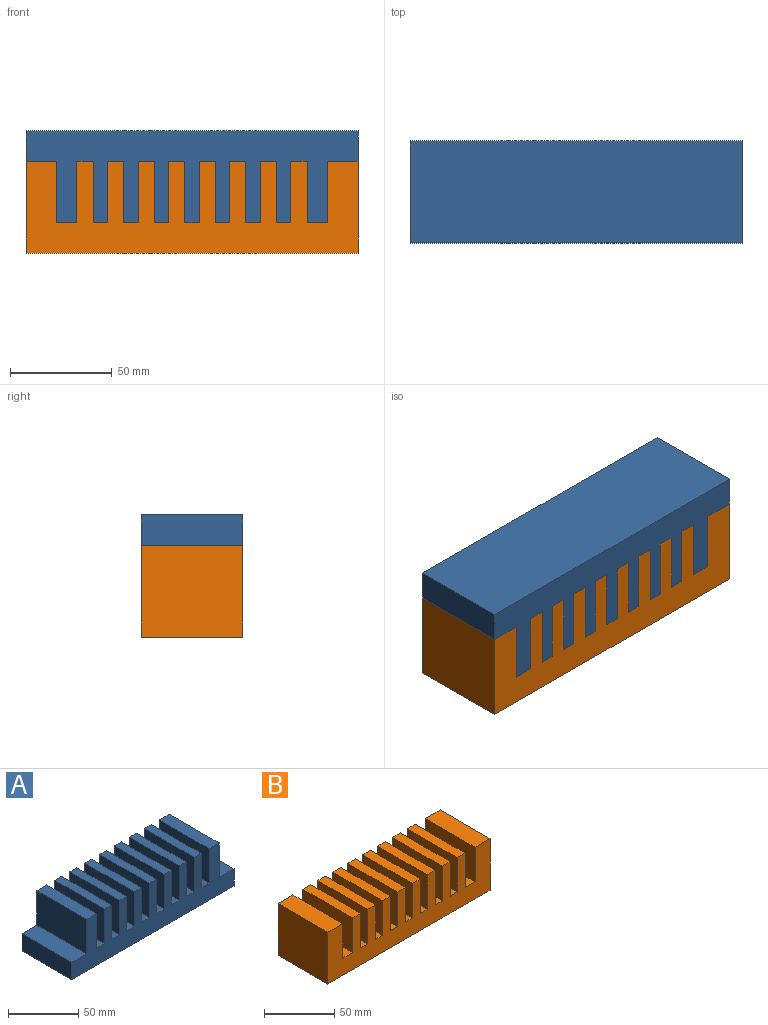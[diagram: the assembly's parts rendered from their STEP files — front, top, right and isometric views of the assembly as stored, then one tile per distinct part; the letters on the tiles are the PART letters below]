
ASSEMBLY  parts=2 mates=1
PART A: 42 faces, bbox 163x50x45 mm
  f0: plane 50x30mm, normal (1,0,0), area 1500mm2, adj f1,f39,f40,f41
  f1: plane 50x7mm, normal (0,0,1), area 350mm2, adj f0,f2,f40,f41
  f2: plane 50x30mm, normal (-1,0,0), area 1500mm2, adj f1,f3,f40,f41
  f3: plane 50x8mm, normal (0,0,1), area 400mm2, adj f2,f4,f40,f41
  f4: plane 50x30mm, normal (1,0,0), area 1500mm2, adj f3,f5,f40,f41
  f5: plane 50x7mm, normal (0,0,1), area 350mm2, adj f4,f6,f40,f41
  f6: plane 50x30mm, normal (-1,0,0), area 1500mm2, adj f5,f7,f40,f41
  f7: plane 50x8mm, normal (0,0,1), area 400mm2, adj f6,f8,f40,f41
  f8: plane 50x30mm, normal (1,0,0), area 1500mm2, adj f7,f9,f40,f41
  f9: plane 50x7mm, normal (0,0,1), area 350mm2, adj f8,f10,f40,f41
  f10: plane 50x30mm, normal (-1,0,0), area 1500mm2, adj f9,f11,f40,f41
  f11: plane 50x8mm, normal (0,0,1), area 400mm2, adj f10,f12,f40,f41
  f12: plane 50x30mm, normal (1,0,0), area 1500mm2, adj f11,f13,f40,f41
  f13: plane 50x7mm, normal (0,0,1), area 350mm2, adj f12,f14,f40,f41
  f14: plane 50x30mm, normal (-1,0,0), area 1500mm2, adj f13,f15,f40,f41
  f15: plane 50x8mm, normal (0,0,1), area 400mm2, adj f14,f16,f40,f41
  f16: plane 50x30mm, normal (1,0,0), area 1500mm2, adj f15,f17,f40,f41
  f17: plane 50x10mm, normal (0,0,1), area 500mm2, adj f16,f18,f40,f41
  f18: plane 50x30mm, normal (-1,0,0), area 1500mm2, adj f17,f19,f40,f41
  f19: plane 50x15mm, normal (0,0,1), area 750mm2, adj f18,f20,f40,f41
  f20: plane 50x15mm, normal (-1,0,0), area 750mm2, adj f19,f21,f40,f41
  f21: plane 163x50mm, normal (0,0,-1), area 8150mm2, adj f20,f22,f40,f41
  f22: plane 50x15mm, normal (1,0,0), area 750mm2, adj f21,f23,f40,f41
  f23: plane 50x15mm, normal (0,0,1), area 750mm2, adj f22,f24,f40,f41
  f24: plane 50x30mm, normal (1,0,0), area 1500mm2, adj f23,f25,f40,f41
  f25: plane 50x10mm, normal (0,0,1), area 500mm2, adj f24,f26,f40,f41
  f26: plane 50x30mm, normal (-1,0,0), area 1500mm2, adj f25,f27,f40,f41
  f27: plane 50x8mm, normal (0,0,1), area 400mm2, adj f26,f28,f40,f41
  f28: plane 50x30mm, normal (1,0,0), area 1500mm2, adj f27,f29,f40,f41
  f29: plane 50x7mm, normal (0,0,1), area 350mm2, adj f28,f30,f40,f41
  f30: plane 50x30mm, normal (-1,0,0), area 1500mm2, adj f29,f31,f40,f41
  f31: plane 50x8mm, normal (0,0,1), area 400mm2, adj f30,f32,f40,f41
  f32: plane 50x30mm, normal (1,0,0), area 1500mm2, adj f31,f33,f40,f41
  f33: plane 50x7mm, normal (0,0,1), area 350mm2, adj f32,f34,f40,f41
  f34: plane 50x30mm, normal (-1,0,0), area 1500mm2, adj f33,f35,f40,f41
  f35: plane 50x8mm, normal (0,0,1), area 400mm2, adj f34,f36,f40,f41
  f36: plane 50x30mm, normal (1,0,0), area 1500mm2, adj f35,f37,f40,f41
  f37: plane 50x7mm, normal (0,0,1), area 350mm2, adj f36,f38,f40,f41
  f38: plane 50x30mm, normal (-1,0,0), area 1500mm2, adj f37,f39,f40,f41
  f39: plane 50x8mm, normal (0,0,1), area 400mm2, adj f0,f38,f40,f41
  f40: plane 163x45mm, normal (0,-1,0), area 4515mm2, adj f0,f1,f2,f3,f4,f5,f6,f7
  f41: plane 163x45mm, normal (0,1,0), area 4515mm2, adj f0,f1,f2,f3,f4,f5,f6,f7
PART B: 42 faces, bbox 163x50x45 mm
  f0: plane 50x7mm, normal (0,0,1), area 350mm2, adj f1,f39,f40,f41
  f1: plane 50x30mm, normal (1,0,0), area 1500mm2, adj f0,f2,f40,f41
  f2: plane 50x8mm, normal (0,0,1), area 400mm2, adj f1,f3,f40,f41
  f3: plane 50x30mm, normal (-1,0,0), area 1500mm2, adj f2,f4,f40,f41
  f4: plane 50x7mm, normal (0,0,1), area 350mm2, adj f3,f5,f40,f41
  f5: plane 50x30mm, normal (1,0,0), area 1500mm2, adj f4,f6,f40,f41
  f6: plane 50x8mm, normal (0,0,1), area 400mm2, adj f5,f7,f40,f41
  f7: plane 50x30mm, normal (-1,0,0), area 1500mm2, adj f6,f8,f40,f41
  f8: plane 50x7mm, normal (0,0,1), area 350mm2, adj f7,f9,f40,f41
  f9: plane 50x30mm, normal (1,0,0), area 1500mm2, adj f8,f10,f40,f41
  f10: plane 50x8mm, normal (0,0,1), area 400mm2, adj f9,f11,f40,f41
  f11: plane 50x30mm, normal (-1,0,0), area 1500mm2, adj f10,f12,f40,f41
  f12: plane 50x7mm, normal (0,0,1), area 350mm2, adj f11,f13,f40,f41
  f13: plane 50x30mm, normal (1,0,0), area 1500mm2, adj f12,f14,f40,f41
  f14: plane 50x8mm, normal (0,0,1), area 400mm2, adj f13,f15,f40,f41
  f15: plane 50x30mm, normal (-1,0,0), area 1500mm2, adj f14,f16,f40,f41
  f16: plane 50x10mm, normal (0,0,1), area 500mm2, adj f15,f17,f40,f41
  f17: plane 50x30mm, normal (1,0,0), area 1500mm2, adj f16,f18,f40,f41
  f18: plane 50x15mm, normal (0,0,1), area 750mm2, adj f17,f19,f40,f41
  f19: plane 50x45mm, normal (-1,0,0), area 2250mm2, adj f18,f20,f40,f41
  f20: plane 163x50mm, normal (0,0,-1), area 8150mm2, adj f19,f21,f40,f41
  f21: plane 50x45mm, normal (1,0,0), area 2250mm2, adj f20,f22,f40,f41
  f22: plane 50x15mm, normal (0,0,1), area 750mm2, adj f21,f23,f40,f41
  f23: plane 50x30mm, normal (-1,0,0), area 1500mm2, adj f22,f24,f40,f41
  f24: plane 50x10mm, normal (0,0,1), area 500mm2, adj f23,f25,f40,f41
  f25: plane 50x30mm, normal (1,0,0), area 1500mm2, adj f24,f26,f40,f41
  f26: plane 50x8mm, normal (0,0,1), area 400mm2, adj f25,f27,f40,f41
  f27: plane 50x30mm, normal (-1,0,0), area 1500mm2, adj f26,f28,f40,f41
  f28: plane 50x7mm, normal (0,0,1), area 350mm2, adj f27,f29,f40,f41
  f29: plane 50x30mm, normal (1,0,0), area 1500mm2, adj f28,f30,f40,f41
  f30: plane 50x8mm, normal (0,0,1), area 400mm2, adj f29,f31,f40,f41
  f31: plane 50x30mm, normal (-1,0,0), area 1500mm2, adj f30,f32,f40,f41
  f32: plane 50x7mm, normal (0,0,1), area 350mm2, adj f31,f33,f40,f41
  f33: plane 50x30mm, normal (1,0,0), area 1500mm2, adj f32,f34,f40,f41
  f34: plane 50x8mm, normal (0,0,1), area 400mm2, adj f33,f35,f40,f41
  f35: plane 50x30mm, normal (-1,0,0), area 1500mm2, adj f34,f36,f40,f41
  f36: plane 50x7mm, normal (0,0,1), area 350mm2, adj f35,f37,f40,f41
  f37: plane 50x30mm, normal (1,0,0), area 1500mm2, adj f36,f38,f40,f41
  f38: plane 50x8mm, normal (0,0,1), area 400mm2, adj f37,f39,f40,f41
  f39: plane 50x30mm, normal (-1,0,0), area 1500mm2, adj f0,f38,f40,f41
  f40: plane 163x45mm, normal (0,-1,0), area 5265mm2, adj f0,f1,f2,f3,f4,f5,f6,f7
  f41: plane 163x45mm, normal (0,1,0), area 5265mm2, adj f0,f1,f2,f3,f4,f5,f6,f7
PLACE A rot(axis=(1,0,0),180deg) t=(-55.22,-89.29,-34.01)mm
PLACE B t=(-55.22,-39.29,-46.51)mm
MATE fastened A.f1 <-> B.f0  axis (0,0,-1) through (-55.22,-64.29,-54.01)mm
